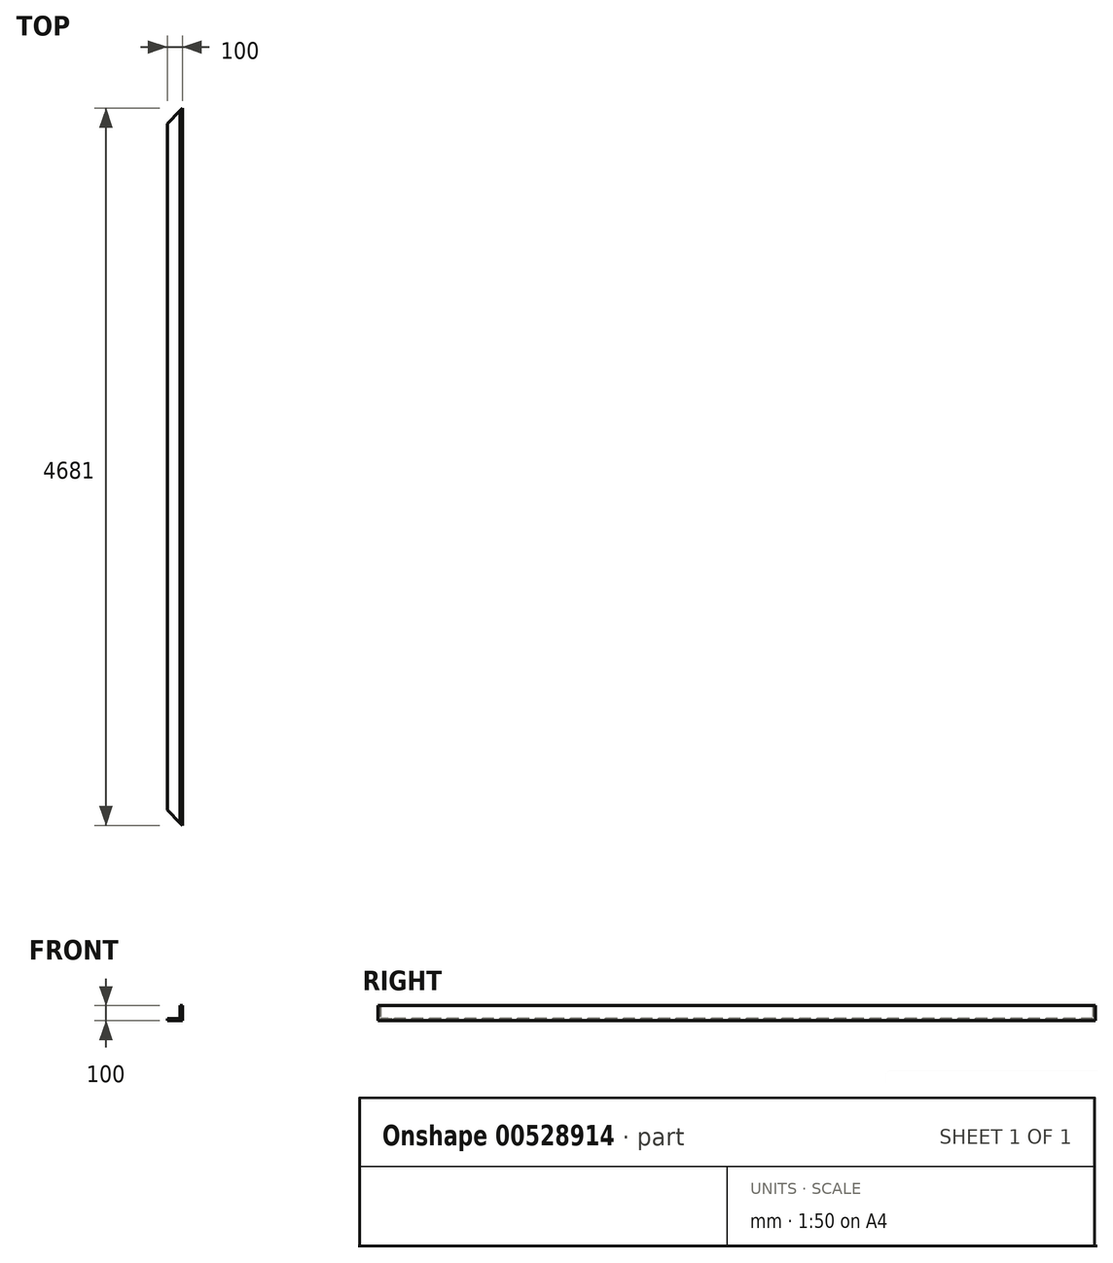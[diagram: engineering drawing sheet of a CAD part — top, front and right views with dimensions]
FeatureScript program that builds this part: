
annotation { "Feature Type Name" : "Feature", "Feature Type Description" : "" }
export const myFeature = defineFeature(function(context is Context, id is Id, definition is map)
    precondition{}
    {
        {
            var Q0;
            Q0=qCreatedBy(makeId("Top.planeOp"),FACE);
            var sketch = newSketch(context, id + "F0", { "sketchPlane" : qUnion([Q0])});
            skLineSegment(sketch, "E0", {"start": v(0, -2340.5) * mm, "end": v(0, 2340.5) * mm});
            skLineSegment(sketch, "E1", {"start": v(-100, -2240.5) * mm, "end": v(-100, 2240.5) * mm});
            skLineSegment(sketch, "E2", {"start": v(0, -2340.5) * mm, "end": v(-100, -2240.5) * mm});
            skLineSegment(sketch, "E3", {"start": v(0, 2340.5) * mm, "end": v(-100, 2240.5) * mm});
            skSolve(sketch);
        }
        {
            var Q0;
            Q0=makeQuery(id+"F0.imprint","IMPRINT",FACE,{"disambiguationData":[TD([[makeQuery(id+"F0.imprint","IMPRINT",EDGE,{"derivedFrom":sQuery(id+"F0.wireOp",EDGE,"E0")}),1.0]])]});
            extrude(context, id + "F1", {"entities" : qUnion([Q0]), "depth" : 15 * mm, "offsetDistance" : 25 * mm});
        }
        {
            var Q0;
            Q0=makeQuery(id+"F1.opExtrude","CAP_FACE",FACE,{"disambiguationData":[OSD([sQuery(id+"F0.wireOp",EDGE,"E0"),sQuery(id+"F0.wireOp",EDGE,"E1"),sQuery(id+"F0.wireOp",EDGE,"E2"),sQuery(id+"F0.wireOp",EDGE,"E3")])],"isStart":false});
            var sketch = newSketch(context, id + "F2", { "sketchPlane" : qUnion([Q0])});
            skLineSegment(sketch, "E4.0", {"start": v(0, -2340.5) * mm, "end": v(0, 2340.5) * mm});
            skLineSegment(sketch, "E5", {"start": v(-15, 2325.5) * mm, "end": v(-15, -2325.5) * mm});
            skLineSegment(sketch, "E6", {"start": v(0, 2340.5) * mm, "end": v(-15, 2325.5) * mm});
            skLineSegment(sketch, "E7", {"start": v(-15, -2325.5) * mm, "end": v(0, -2340.5) * mm});
            skSolve(sketch);
        }
        {
            var Q0;
            Q0=makeQuery(id+"F2.imprint","IMPRINT",FACE,{"disambiguationData":[TD([[makeQuery(id+"F2.imprint","IMPRINT",EDGE,{"derivedFrom":sQuery(id+"F2.wireOp",EDGE,"E4.0")}),1.0]])]});
            extrude(context, id + "F3", {"entities" : qUnion([Q0]), "operationType" : NewBodyOperationType.ADD, "depth" : (100 - 15) * mm, "offsetDistance" : 25 * mm});
        }
    });
